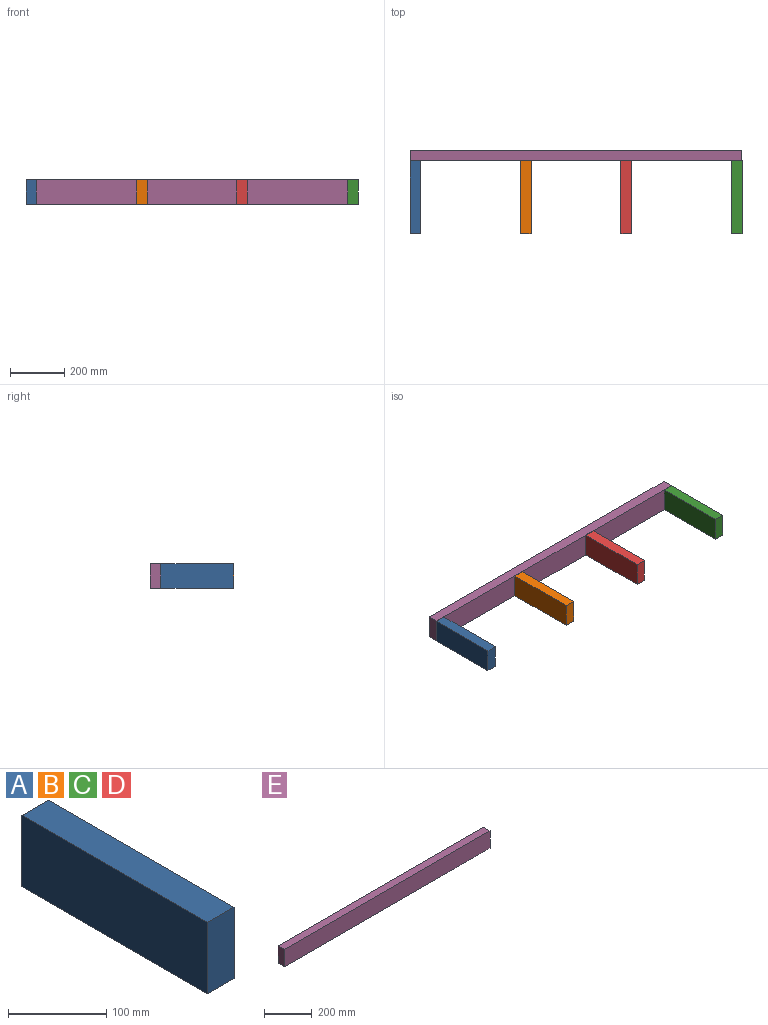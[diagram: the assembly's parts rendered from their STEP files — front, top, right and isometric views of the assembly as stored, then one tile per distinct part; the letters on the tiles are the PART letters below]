
ASSEMBLY  parts=5 mates=4
PART A: 6 faces, bbox 38.1x266.7x88.9 mm
  f0: plane 266.7x38.1mm, normal (0,0,-1), area 10161.3mm2, adj f1,f3,f4,f5
  f1: plane 266.7x88.9mm, normal (1,0,0), area 23709.6mm2, adj f0,f2,f4,f5
  f2: plane 266.7x38.1mm, normal (0,0,1), area 10161.3mm2, adj f1,f3,f4,f5
  f3: plane 266.7x88.9mm, normal (-1,0,0), area 23709.6mm2, adj f0,f2,f4,f5
  f4: plane 88.9x38.1mm, normal (0,-1,0), area 3387.1mm2, adj f0,f1,f2,f3
  f5: plane 88.9x38.1mm, normal (0,1,0), area 3387.1mm2, adj f0,f1,f2,f3
PART B: same geometry as A
PART C: same geometry as A
PART D: same geometry as A
PART E: 6 faces, bbox 1219.2x38.1x88.9 mm
  f0: plane 88.9x38.1mm, normal (1,0,0), area 3387.1mm2, adj f1,f3,f4,f5
  f1: plane 1219.2x38.1mm, normal (0,0,1), area 46451.5mm2, adj f0,f2,f4,f5
  f2: plane 88.9x38.1mm, normal (-1,0,0), area 3387.1mm2, adj f1,f3,f4,f5
  f3: plane 1219.2x38.1mm, normal (0,0,-1), area 46451.5mm2, adj f0,f2,f4,f5
  f4: plane 1219.2x88.9mm, normal (0,-1,0), area 108386.9mm2, adj f0,f1,f2,f3
  f5: plane 1219.2x88.9mm, normal (0,1,0), area 108386.9mm2, adj f0,f1,f2,f3
PLACE A t=(-590.55,0,0)mm
PLACE B t=(-184.15,0,0)mm
PLACE C t=(590.55,0,0)mm
PLACE D t=(184.15,0,0)mm
PLACE E at identity fixed
MATE fastened C.f5 <-> E.f4  axis (0,1,0) through (609.6,-38.1,-44.45)mm
MATE fastened B.f5 <-> E.f4  axis (0,1,0) through (-203.2,-38.1,-44.45)mm
MATE fastened A.f5 <-> E.f4  axis (0,1,0) through (-609.6,-38.1,-44.45)mm
MATE fastened D.f5 <-> E.f4  axis (0,1,0) through (203.2,-38.1,-44.45)mm
